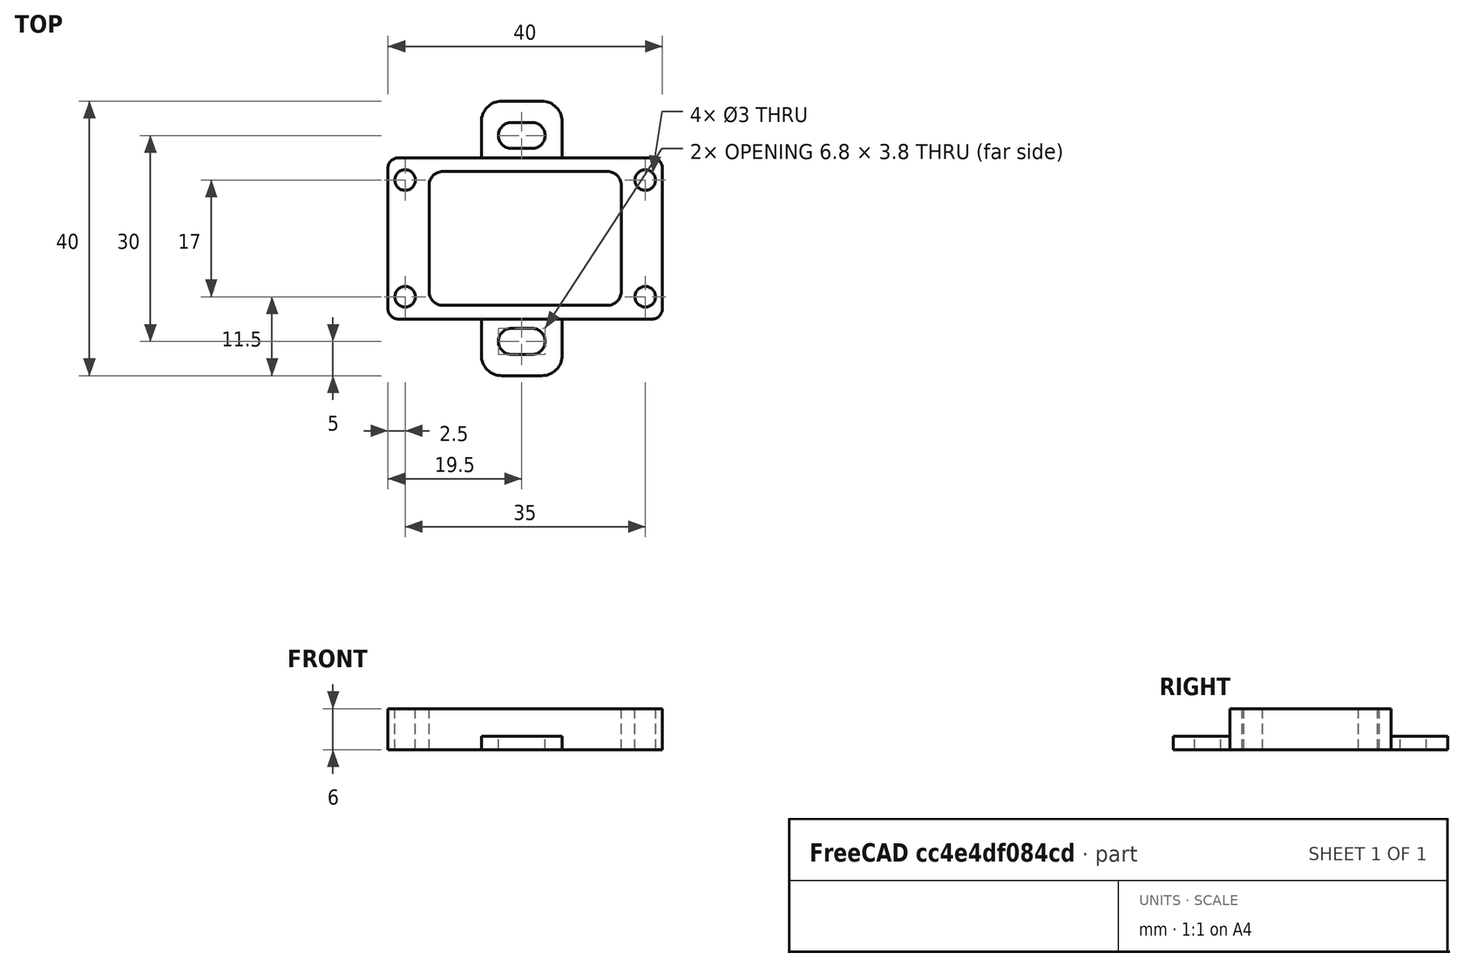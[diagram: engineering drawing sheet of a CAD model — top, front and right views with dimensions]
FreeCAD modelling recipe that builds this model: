
FCSTD DOCUMENT  (FreeCAD 0.19R23578 (Git))
Label: stetdown_lm25775
License: All rights reserved
LicenseURL: http://en.wikipedia.org/wiki/All_rights_reserved
objects: Part::Box×2, Part::Fillet×2, Part::MultiFuse×2, Spreadsheet::Sheet×1, Part::Cylinder×1, Part::FeaturePython×1, Part::Feature×1, Part::Cut×1, App::Part×1
note: 10 computed .brp shape members not serialized (recipe doc carries the construction recipe); baked Part::Feature solids carry a one-line shape summary decoded from their .brp

FEATURE [Spreadsheet::Sheet] Spreadsheet  label="p"
  cells = A1=hole_x_dist; B1(hole_x_dist)=35; A2=hole_y_dist; B2(hole_y_dist)=17; A3=pcb_under; B3(pcb_under)=6; A4=pcb_x; B4(pcb_x)=40; A5=pcb_y; B5(pcb_y)=23.5; A6=hole_r; B6(hole_r)=1.5; A7=under_pcb_border_x; B7(under_pcb_border_x)=6; A8=under_pcb_border_y; B8(under_pcb_border_y)=2
FEATURE [Part::Box] Box  label="bottom cube"
  AttacherType = Attacher::AttachEngine3D
  Height = 6
  Length = 40
  Width = 23.5
  expr: Width = <<p>>.pcb_y
  expr: Length = <<p>>.pcb_x
  expr: Height = <<p>>.pcb_under
FEATURE [Part::Box] Box001  label="bottom extraction cube"
  AttacherType = Attacher::AttachEngine3D
  Height = 10
  Length = 28
  Placement = pos=(6,2,0) rot=(0,0,1;0rad)
  Width = 19.5
  expr: .Placement.Base.y = Spreadsheet.under_pcb_border_y
  expr: .Placement.Base.x = Spreadsheet.under_pcb_border_x
  expr: Length = <<p>>.pcb_x - <<p>>.under_pcb_border_x * 2
  expr: Width = <<p>>.pcb_y - <<p>>.under_pcb_border_y * 2
FEATURE [Part::Cylinder] Cylinder  label="pcb hole"
  Angle = 360
  AttacherType = Attacher::AttachEngine3D
  Height = 10
  Radius = 1.5
  expr: Radius = <<p>>.hole_r
FEATURE [Part::FeaturePython] Array001  label="hole array"  # Draft array (typed FeaturePython)
  Angle = 360
  ArrayType = 0
  Axis = (0,0,1)
  Base = -> Cylinder
  Center = (0,0,0)
  Fuse = false
  IntervalAxis = (0,0,0)
  IntervalX = (35,0,0)
  IntervalY = (0,17,0)
  IntervalZ = (0,0,1)
  NumberPolar = 1
  NumberX = 2
  NumberY = 2
  NumberZ = 1
  Placement = pos=(2.5,3.25,0) rot=(0,0,1;0rad)
  expr: .IntervalY.y = <<p>>.hole_y_dist
  expr: .IntervalX.x = <<p>>.hole_x_dist
  expr: .Placement.Base.x = (<<p>>.pcb_x - <<p>>.hole_x_dist) / 2
  expr: .Placement.Base.y = (<<p>>.pcb_y - <<p>>.hole_y_dist) / 2
FEATURE [Part::Fillet] Fillet001  label="bottom cube fillet"
  Base = -> Box
  Edges = 4 edges r=1.5: [Edge1,Edge3,Edge5,Edge7]
FEATURE [Part::Fillet] Fillet  label="bottom extraction cube fillet"
  Base = -> Box001
  Edges = 4 edges r=2: [Edge1,Edge3,Edge5,Edge7]
FEATURE [Part::MultiFuse] Fusion  label="bottom extraction"
  Shapes = -> [Array001,Fillet]
FEATURE [Part::Feature] Cut002002  label="attach plane y dir002"
  Placement = pos=(13.6,-8.25,0) rot=(0,0,1;0rad)
  shape: bbox 11.8 x 40 x 2 mm, 20 faces (baked)
FEATURE [Part::MultiFuse] Fusion002  label="bottom fusion"
  Shapes = -> [Fillet001,Cut002002]
FEATURE [Part::Cut] Cut  label="pcb box cut"
  Base = -> Fusion002
  Tool = -> Fusion
FEATURE [App::Part] Part  label="stepup_stepdown part"
  Group = -> [Cut]
  Origin = -> Origin
